# Revit family: Yuma Surface 250
name_source: partatom
category: Lighting Fixtures
revit_build: Autodesk Revit 2018 (Build: 20170223_1515(x64)
units: mm (PartAtom-declared; Revit-internal decimal feet)

## family parameters
Always vertical = Yes
Cut with Voids When Loaded = No
Host = Ceiling
Light Source = Yes
OmniClass Number = 23.80.70.11
OmniClass Title = Luminaries for Internal Lighting
Part Type = Normal
Room Calculation Point = No
Round Connector Dimension = Use Diameter
Shared = No

## types (2) — shared parameters
Apparent Load = 11 VA
Color Filter = 16777215
Dimmable = Yes
Dimming Lamp Color Temperature Shift = <None>
Dimming Method = Phase - Trailing Edge
Driver Included = Yes
Driver Required = No
Electrical Class = 1
Lamp = LED
Light Source Fixed = Integral LED
Location Rating = IP20
Main Material = Metal - Aluminium
Power (Watts) = 10.3
Product Location = Indoor
Product Name = Yuma Surface 250
Tilt Angle = 90.00°

## per-type parameters (varying)
| type | Efficacy (lm/w) | Main Finish | Photometric Web File | Product SKU |
| White bezel version only | 61 | Textured White | GNC-3753 Yuma 70 White.ies | 1399013 |
| Black bezel version | 52 | Various | GNC-3752 Yuma 70 Black.ies | 1399XXX |

## geometry (parser evidence)
native form markers: Sweep x1
no freeform markers — native parametric forms only
